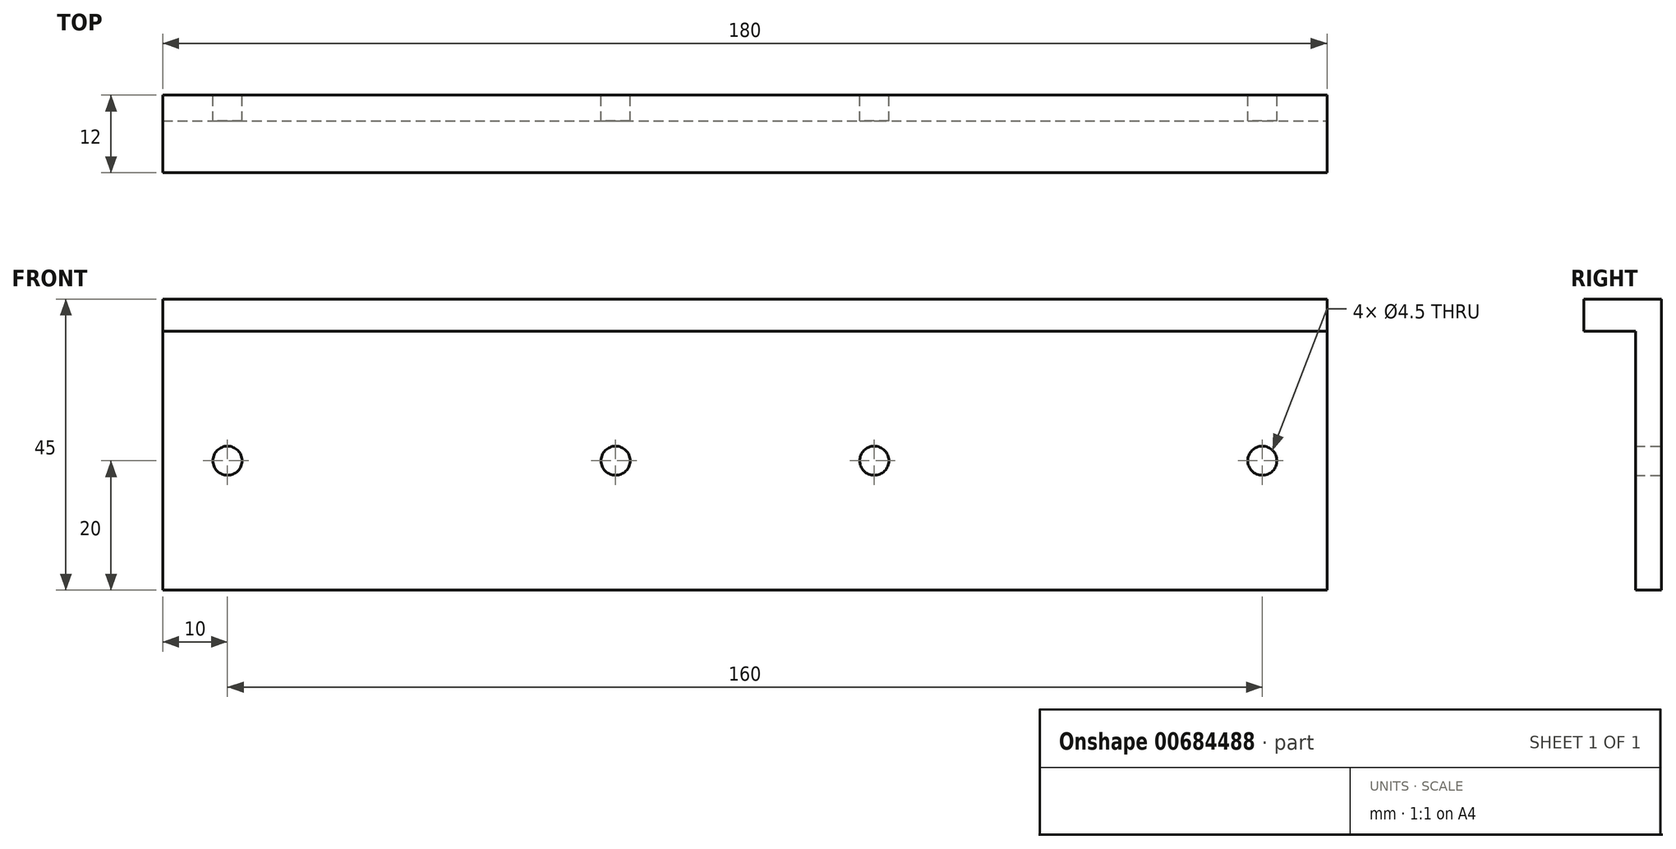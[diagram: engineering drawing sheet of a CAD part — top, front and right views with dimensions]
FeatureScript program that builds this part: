
annotation { "Feature Type Name" : "Feature", "Feature Type Description" : "" }
export const myFeature = defineFeature(function(context is Context, id is Id, definition is map)
    precondition{}
    {
        {
            var Q0;
            Q0=qCreatedBy(makeId("Front.planeOp"),FACE);
            var sketch = newSketch(context, id + "F0", { "sketchPlane" : qUnion([Q0])});
            skLineSegment(sketch, "E0.bottom", {"start": v(-90, 25) * mm, "end": v(90, 25) * mm});
            skLineSegment(sketch, "E0.top", {"start": v(-90, -20) * mm, "end": v(90, -20) * mm});
            skLineSegment(sketch, "E0.left", {"start": v(-90, 25) * mm, "end": v(-90, -20) * mm});
            skLineSegment(sketch, "E0.right", {"start": v(90, 25) * mm, "end": v(90, -20) * mm});
            skCircle(sketch, "E1", {"center": v(-80, 0) * mm, "radius": 2.25 * mm});
            skCircle(sketch, "E2", {"center": v(-20, 0) * mm, "radius": 2.25 * mm});
            skCircle(sketch, "E3", {"center": v(20, 0) * mm, "radius": 2.25 * mm});
            skCircle(sketch, "E4", {"center": v(80, 0) * mm, "radius": 2.25 * mm});
            skSolve(sketch);
        }
        {
            var Q0;
            Q0=makeQuery(id+"F0.imprint","IMPRINT",FACE,{"disambiguationData":[TD([[makeQuery(id+"F0.imprint","IMPRINT",EDGE,{"derivedFrom":sQuery(id+"F0.wireOp",EDGE,"E0.bottom")}),-1.0]])]});
            extrude(context, id + "F1", {"entities" : qUnion([Q0]), "depth" : 4 * mm, "offsetDistance" : 25 * mm});
        }
        {
            var Q0;
            Q0=makeQuery(id+"F1.opExtrude","CAP_FACE",FACE,{"disambiguationData":[OSD([sQuery(id+"F0.wireOp",EDGE,"E0.bottom"),sQuery(id+"F0.wireOp",EDGE,"E0.top"),sQuery(id+"F0.wireOp",EDGE,"E0.left"),sQuery(id+"F0.wireOp",EDGE,"E0.right"),sQuery(id+"F0.wireOp",EDGE,"E1"),sQuery(id+"F0.wireOp",EDGE,"E2"),sQuery(id+"F0.wireOp",EDGE,"E3"),sQuery(id+"F0.wireOp",EDGE,"E4")])],"isStart":false});
            var sketch = newSketch(context, id + "F2", { "sketchPlane" : qUnion([Q0])});
            skLineSegment(sketch, "E5.bottom", {"start": v(-90, 25) * mm, "end": v(90, 25) * mm});
            skLineSegment(sketch, "E5.top", {"start": v(-90, 20) * mm, "end": v(90, 20) * mm});
            skLineSegment(sketch, "E5.left", {"start": v(-90, 25) * mm, "end": v(-90, 20) * mm});
            skLineSegment(sketch, "E5.right", {"start": v(90, 25) * mm, "end": v(90, 20) * mm});
            skSolve(sketch);
        }
        {
            var Q0;
            Q0=makeQuery(id+"F2.imprint","IMPRINT",FACE,{"disambiguationData":[TD([[makeQuery(id+"F2.imprint","IMPRINT",EDGE,{"derivedFrom":sQuery(id+"F2.wireOp",EDGE,"E5.bottom")}),-1.0]])]});
            extrude(context, id + "F3", {"entities" : qUnion([Q0]), "operationType" : NewBodyOperationType.ADD, "depth" : 8 * mm, "offsetDistance" : 25 * mm});
        }
    });
